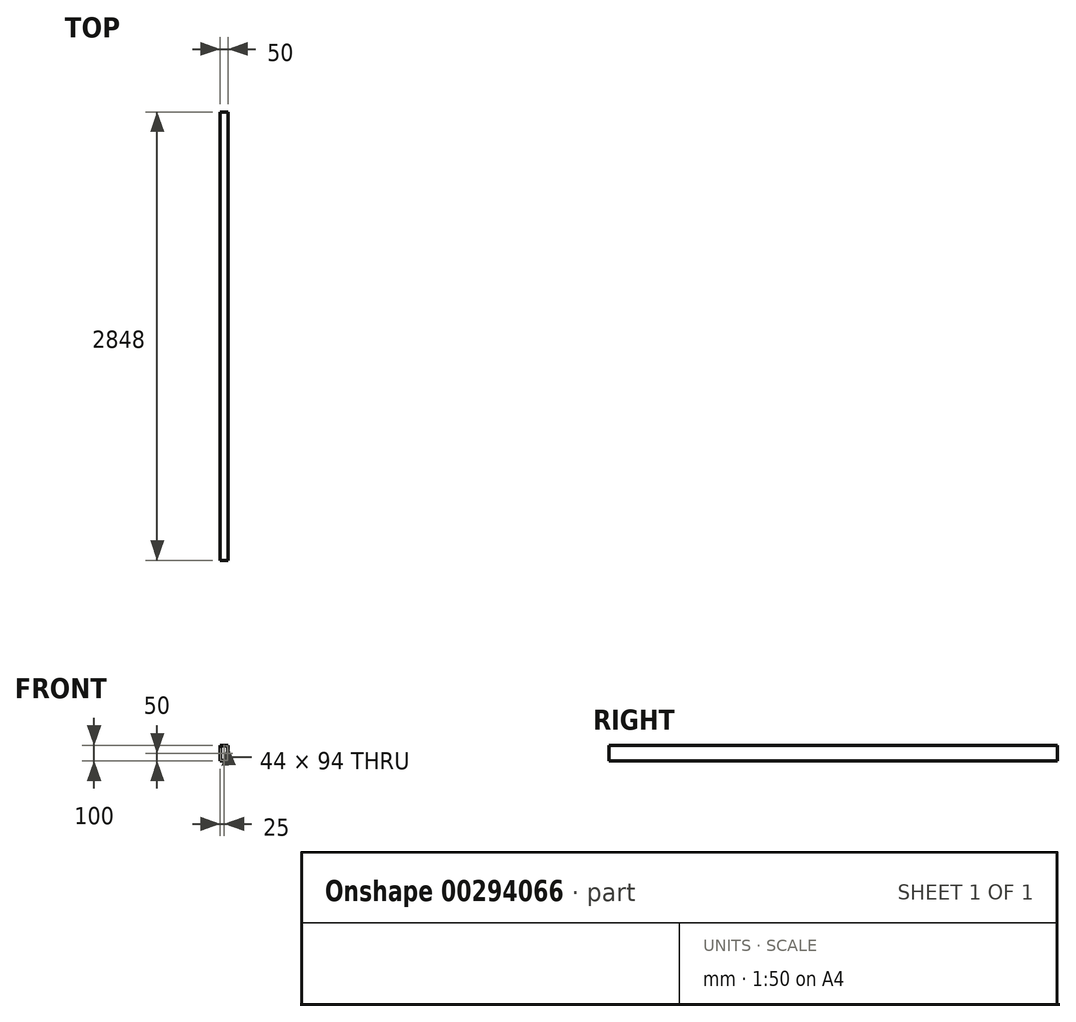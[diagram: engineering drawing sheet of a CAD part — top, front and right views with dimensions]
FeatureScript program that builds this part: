
annotation { "Feature Type Name" : "Feature", "Feature Type Description" : "" }
export const myFeature = defineFeature(function(context is Context, id is Id, definition is map)
    precondition{}
    {
        {
            var Q0;
            Q0=qCreatedBy(makeId("Front.planeOp"),FACE);
            var sketch = newSketch(context, id + "F0", { "sketchPlane" : qUnion([Q0])});
            skLineSegment(sketch, "E0", {"start": v(0, 0) * mm, "end": v(0, 100) * mm});
            skLineSegment(sketch, "E1", {"start": v(0, 100) * mm, "end": v(50, 100) * mm});
            skLineSegment(sketch, "E2", {"start": v(50, 100) * mm, "end": v(50, 0) * mm});
            skLineSegment(sketch, "E3", {"start": v(50, 0) * mm, "end": v(0, 0) * mm});
            skLineSegment(sketch, "E4", {"start": v(3, 97) * mm, "end": v(3, 3) * mm});
            skLineSegment(sketch, "E5", {"start": v(3, 3) * mm, "end": v(47, 3) * mm});
            skLineSegment(sketch, "E6", {"start": v(47, 3) * mm, "end": v(47, 97) * mm});
            skLineSegment(sketch, "E7", {"start": v(3, 97) * mm, "end": v(47, 97) * mm});
            skSolve(sketch);
        }
        {
            var Q0;
            Q0=makeQuery(id+"F0.imprint","IMPRINT",FACE,{"disambiguationData":[TD([[makeQuery(id+"F0.imprint","IMPRINT",EDGE,{"derivedFrom":sQuery(id+"F0.wireOp",EDGE,"E0")}),-1.0]])]});
            extrude(context, id + "F1", {"entities" : qUnion([Q0]), "depth" : 2848 * mm});
        }
    });
